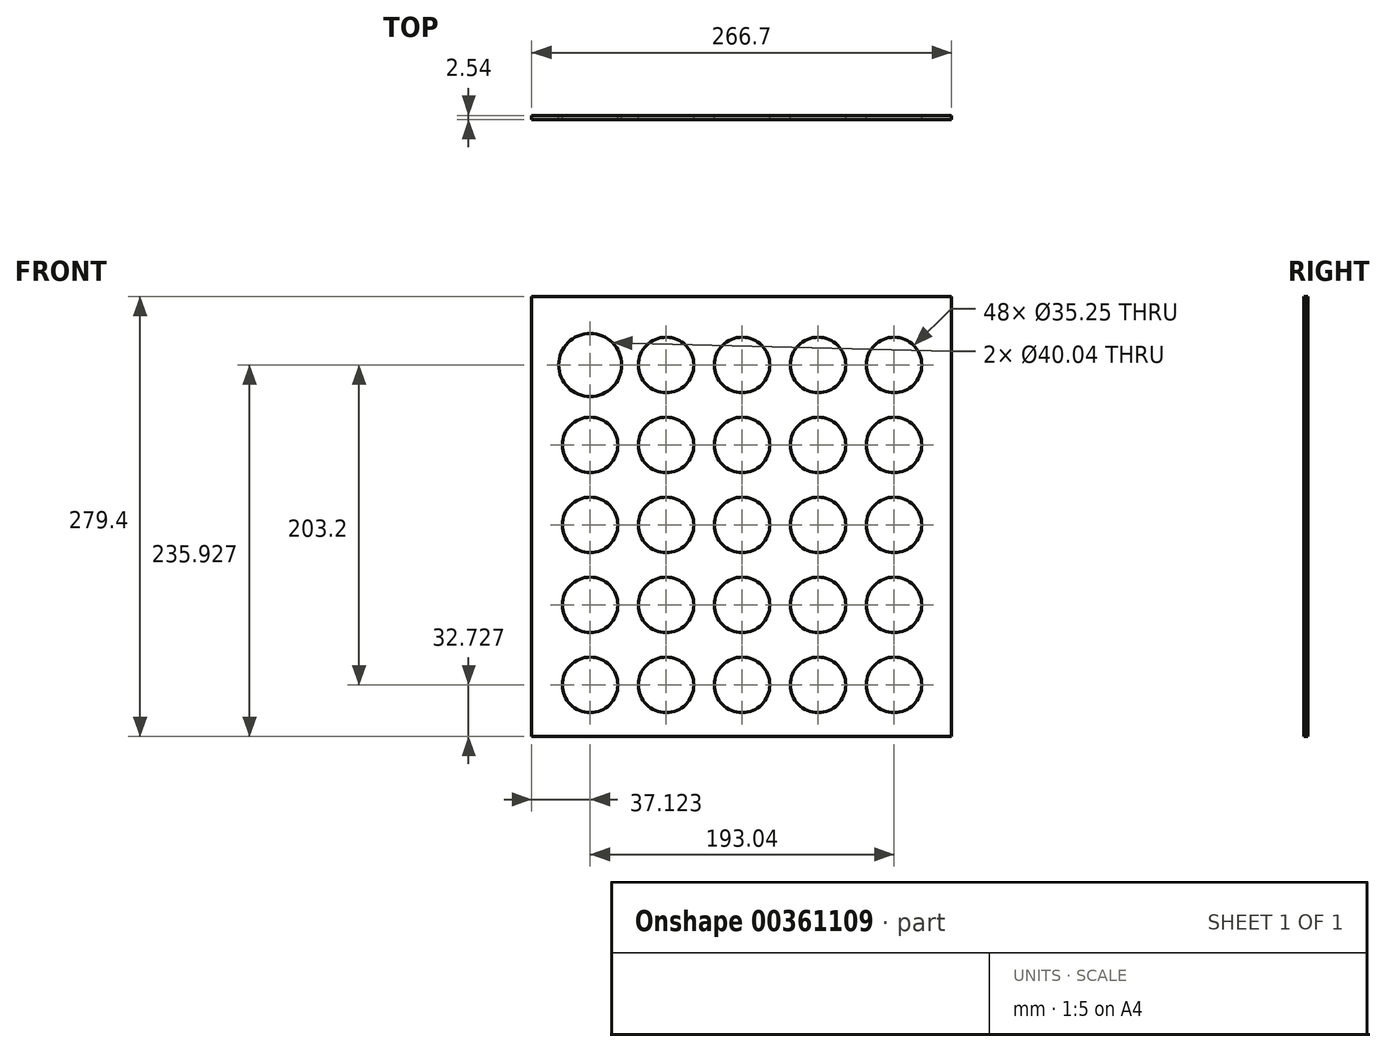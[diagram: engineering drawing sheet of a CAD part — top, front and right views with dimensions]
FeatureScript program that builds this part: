
annotation { "Feature Type Name" : "Feature", "Feature Type Description" : "" }
export const myFeature = defineFeature(function(context is Context, id is Id, definition is map)
    precondition{}
    {
        {
            var Q0;
            Q0=qCreatedBy(makeId("Front.planeOp"),FACE);
            var sketch = newSketch(context, id + "F0", { "sketchPlane" : qUnion([Q0])});
            skLineSegment(sketch, "E0.bottom", {"start": v(-105.95, 167.98) * mm, "end": v(160.75, 167.98) * mm});
            skLineSegment(sketch, "E0.top", {"start": v(-105.95, -111.42) * mm, "end": v(160.75, -111.42) * mm});
            skLineSegment(sketch, "E0.left", {"start": v(-105.95, 167.98) * mm, "end": v(-105.95, -111.42) * mm});
            skLineSegment(sketch, "E0.right", {"start": v(160.75, 167.98) * mm, "end": v(160.75, -111.42) * mm});
            skCircle(sketch, "E1", {"center": v(-68.83, 124.5) * mm, "radius": 20.02 * mm});
            skCircle(sketch, "E2", {"center": v(-68.83, 124.5) * mm, "radius": 17.62 * mm});
            skCircle(sketch, "E3.0.1.0", {"center": v(-68.83, 73.7) * mm, "radius": 17.62 * mm});
            skCircle(sketch, "E3.0.2.0", {"center": v(-68.83, 22.9) * mm, "radius": 17.62 * mm});
            skCircle(sketch, "E3.0.3.0", {"center": v(-68.83, -27.9) * mm, "radius": 17.62 * mm});
            skCircle(sketch, "E3.0.4.0", {"center": v(-68.83, -78.7) * mm, "radius": 17.62 * mm});
            skCircle(sketch, "E3.1.0.0", {"center": v(-20.57, 124.5) * mm, "radius": 17.62 * mm});
            skCircle(sketch, "E3.1.1.0", {"center": v(-20.57, 73.7) * mm, "radius": 17.62 * mm});
            skCircle(sketch, "E3.1.2.0", {"center": v(-20.57, 22.9) * mm, "radius": 17.62 * mm});
            skCircle(sketch, "E3.1.3.0", {"center": v(-20.57, -27.9) * mm, "radius": 17.62 * mm});
            skCircle(sketch, "E3.1.4.0", {"center": v(-20.57, -78.7) * mm, "radius": 17.62 * mm});
            skCircle(sketch, "E3.2.0.0", {"center": v(27.7, 124.5) * mm, "radius": 17.62 * mm});
            skCircle(sketch, "E3.2.1.0", {"center": v(27.7, 73.7) * mm, "radius": 17.62 * mm});
            skCircle(sketch, "E3.2.2.0", {"center": v(27.7, 22.9) * mm, "radius": 17.62 * mm});
            skCircle(sketch, "E3.2.3.0", {"center": v(27.7, -27.9) * mm, "radius": 17.62 * mm});
            skCircle(sketch, "E3.2.4.0", {"center": v(27.7, -78.7) * mm, "radius": 17.62 * mm});
            skCircle(sketch, "E3.3.0.0", {"center": v(75.95, 124.5) * mm, "radius": 17.62 * mm});
            skCircle(sketch, "E3.3.1.0", {"center": v(75.95, 73.7) * mm, "radius": 17.62 * mm});
            skCircle(sketch, "E3.3.2.0", {"center": v(75.95, 22.9) * mm, "radius": 17.62 * mm});
            skCircle(sketch, "E3.3.3.0", {"center": v(75.95, -27.9) * mm, "radius": 17.62 * mm});
            skCircle(sketch, "E3.3.4.0", {"center": v(75.95, -78.7) * mm, "radius": 17.62 * mm});
            skCircle(sketch, "E3.4.0.0", {"center": v(124.21, 124.5) * mm, "radius": 17.62 * mm});
            skCircle(sketch, "E3.4.1.0", {"center": v(124.21, 73.7) * mm, "radius": 17.62 * mm});
            skCircle(sketch, "E3.4.2.0", {"center": v(124.21, 22.9) * mm, "radius": 17.62 * mm});
            skCircle(sketch, "E3.4.3.0", {"center": v(124.21, -27.9) * mm, "radius": 17.62 * mm});
            skCircle(sketch, "E3.4.4.0", {"center": v(124.21, -78.7) * mm, "radius": 17.62 * mm});
            skLineSegment(sketch, "E3.direction1", {"start": v(-68.83, 124.5) * mm, "end": v(-20.57, 124.5) * mm, "construction": true});
            skLineSegment(sketch, "E3.direction2", {"start": v(-68.83, 124.5) * mm, "end": v(-68.83, 73.7) * mm, "construction": true});
            skSolve(sketch);
        }
        {
            var Q0;
            Q0=qSketchRegion(id+"F0",true);
            extrude(context, id + "F1", {"entities" : qUnion([Q0]), "depth" : 2.54 * mm});
        }
        {
            var Q0;
            Q0 = qSketchRegion(id + "F0", true);
            extrude(context, id + "F2", {"entities" : qUnion([Q0]), "operationType" : NewBodyOperationType.ADD, "depth" : 1.27 * mm});
        }
        {
            var Q0;
            Q0=makeQuery(id+"F0.imprint","IMPRINT",FACE,{"disambiguationData":[TD([[makeQuery(id+"F0.imprint","IMPRINT",EDGE,{"derivedFrom":sQuery(id+"F0.wireOp",EDGE,"E0.bottom")}),-1.0]])]});
            extrude(context, id + "F3", {"entities" : qUnion([Q0]), "depth" : 0.25 * mm});
        }
    });
